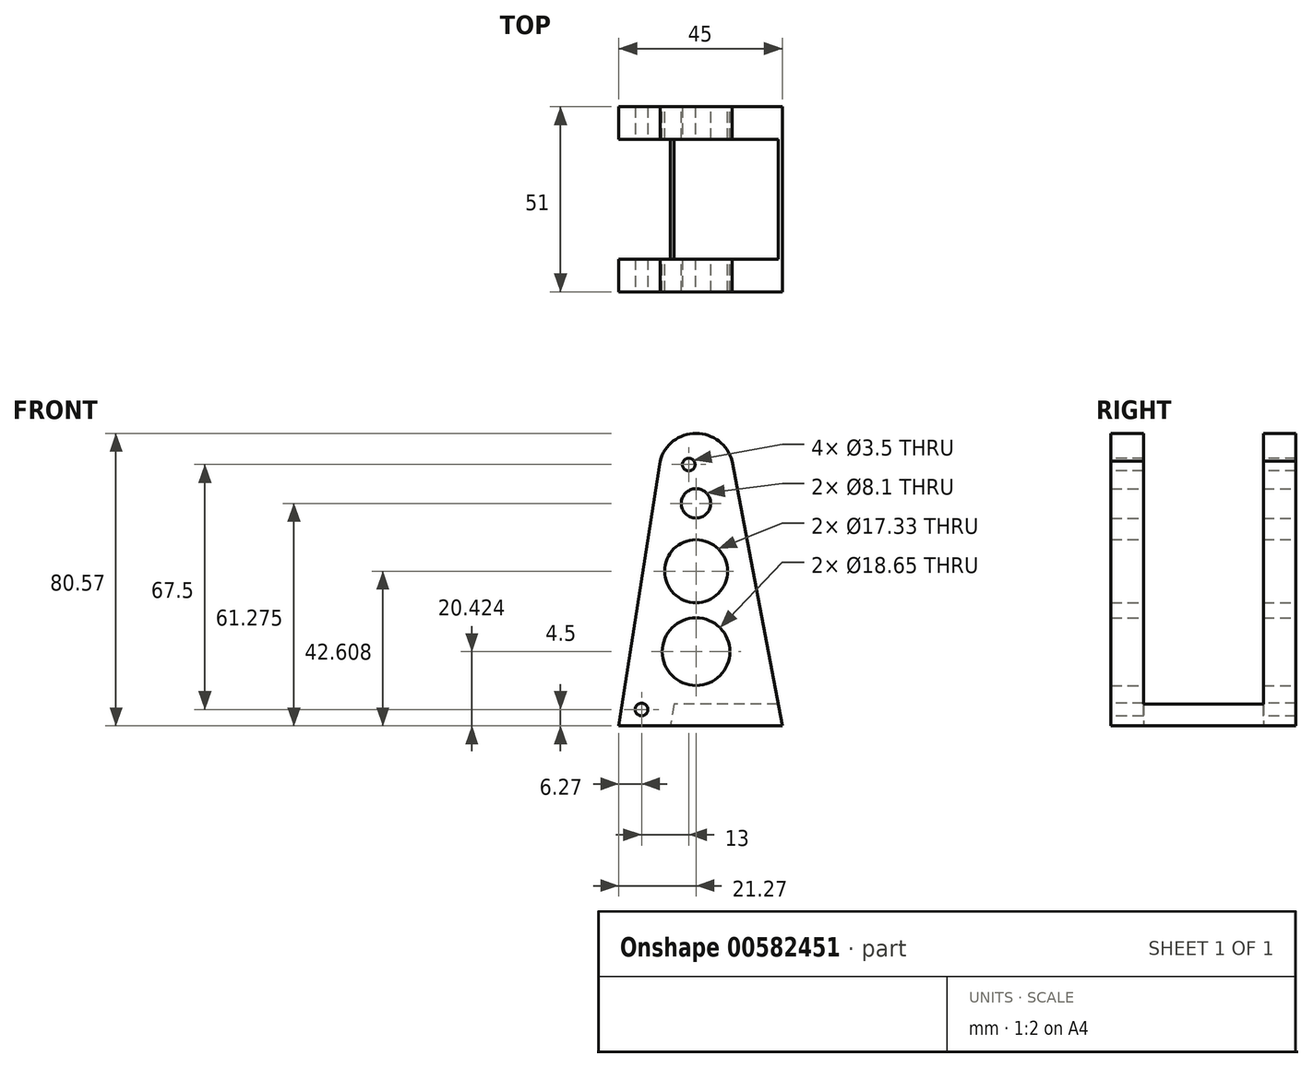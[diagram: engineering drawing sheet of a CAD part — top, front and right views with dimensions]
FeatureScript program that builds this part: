
annotation { "Feature Type Name" : "Feature", "Feature Type Description" : "" }
export const myFeature = defineFeature(function(context is Context, id is Id, definition is map)
    precondition{}
    {
        {
            var Q0;
            Q0=qCreatedBy(makeId("Front.planeOp"),FACE);
            var sketch = newSketch(context, id + "F0", { "sketchPlane" : qUnion([Q0])});
            skLineSegment(sketch, "E0", {"start": v(23.73, 0) * mm, "end": v(9.93, 72.97) * mm});
            skLineSegment(sketch, "E1", {"start": v(23.73, 0) * mm, "end": v(-21.27, 0) * mm});
            skLineSegment(sketch, "E2", {"start": v(-21.27, 0) * mm, "end": v(-9.93, 72.97) * mm});
            skArc(sketch, "E3", {"start": v(9.93, 72.97) * mm, "mid": v(0, 80.57) * mm, "end": v(-9.93, 72.97) * mm});
            skSolve(sketch);
        }
        {
            var Q0;
            Q0 = qSketchRegion(id + "F0", true);
            extrude(context, id + "F1", {"entities" : qUnion([Q0]), "endBound" : BoundingType.SYMMETRIC, "depth" : 51 * mm, "offsetDistance" : 25 * mm});
        }
        {
            var Q0;
            Q0=qCreatedBy(makeId("Front.planeOp"),FACE);
            var sketch = newSketch(context, id + "F2", { "sketchPlane" : qUnion([Q0])});
            skLineSegment(sketch, "E4", {"start": v(30, 6) * mm, "end": v(-6.1, 6) * mm});
            skLineSegment(sketch, "E5", {"start": v(-6.1, 6) * mm, "end": v(-7.03, 0) * mm});
            skLineSegment(sketch, "E6", {"start": v(-7.03, 0) * mm, "end": v(-30, 0) * mm});
            skLineSegment(sketch, "E7", {"start": v(-30, 0) * mm, "end": v(-30, 90) * mm});
            skLineSegment(sketch, "E8", {"start": v(-30, 90) * mm, "end": v(20, 90) * mm});
            skLineSegment(sketch, "E9", {"start": v(20, 90) * mm, "end": v(30, 6) * mm});
            skSolve(sketch);
        }
        {
            var Q0;
            Q0 = qSketchRegion(id + "F2", true);
            extrude(context, id + "F3", {"entities" : qUnion([Q0]), "endBound" : BoundingType.SYMMETRIC, "depth" : 33 * mm, "offsetDistance" : 25 * mm});
        }
        {
            var Q0;
            Q0=makeQuery(id+"F3.opExtrude","SWEPT_BODY",BODY,{"disambiguationData":[OSD([sQuery(id+"F2.wireOp",EDGE,"E4"),sQuery(id+"F2.wireOp",EDGE,"E5"),sQuery(id+"F2.wireOp",EDGE,"E6"),sQuery(id+"F2.wireOp",EDGE,"E7"),sQuery(id+"F2.wireOp",EDGE,"E8"),sQuery(id+"F2.wireOp",EDGE,"E9")])]});
            var Q1;
            Q1=makeQuery(id+"F1.opExtrude","SWEPT_BODY",BODY,{"disambiguationData":[OSD([sQuery(id+"F0.wireOp",EDGE,"E0"),sQuery(id+"F0.wireOp",EDGE,"E1"),sQuery(id+"F0.wireOp",EDGE,"E2"),sQuery(id+"F0.wireOp",EDGE,"E3")])]});
            booleanBodies(context, id + "F4", {"operationType" : BooleanOperationType.SUBTRACTION, "tools" : qUnion([Q0]), "targets" : qUnion([Q1])});
        }
        {
            var Q0;
            Q0=makeQuery(id+"F1.opExtrude","CAP_FACE",FACE,{"disambiguationData":[OSD([sQuery(id+"F0.wireOp",EDGE,"E0"),sQuery(id+"F0.wireOp",EDGE,"E1"),sQuery(id+"F0.wireOp",EDGE,"E2"),sQuery(id+"F0.wireOp",EDGE,"E3")])],"isStart":false});
            var sketch = newSketch(context, id + "F5", { "sketchPlane" : qUnion([Q0])});
            skLineSegment(sketch, "E10.bottom", {"start": v(-15, 4.5) * mm, "end": v(-2, 4.5) * mm});
            skLineSegment(sketch, "E10.top", {"start": v(-15, 72) * mm, "end": v(-2, 72) * mm});
            skLineSegment(sketch, "E10.left", {"start": v(-15, 4.5) * mm, "end": v(-15, 72) * mm});
            skLineSegment(sketch, "E10.right", {"start": v(-2, 4.5) * mm, "end": v(-2, 72) * mm});
            skSolve(sketch);
        }
        {
            var Q0;
            Q0=sQuery(id+"F5.wireOp",VERTEX,"E10.top.end");
            var Q1;
            Q1=sQuery(id+"F5.wireOp",VERTEX,"E10.left.start");
            var Q2;
            Q2=makeQuery(id+"F1.opExtrude","SWEPT_BODY",BODY,{"disambiguationData":[OSD([sQuery(id+"F0.wireOp",EDGE,"E0"),sQuery(id+"F0.wireOp",EDGE,"E1"),sQuery(id+"F0.wireOp",EDGE,"E2"),sQuery(id+"F0.wireOp",EDGE,"E3")])]});
            hole(context, id + "F6", {"style" : HoleStyle.SIMPLE, "endStyle" : HoleEndStyle.THROUGH, "holeDiameter" : 3.5 * mm, "majorDiameter" : 5 * mm, "tappedDepth" : 12 * mm, "tapClearance" : 3, "locations" : qUnion([Q0, Q1]), "scope" : qUnion([Q2])});
        }
        {
            var Q0;
            Q0=qCreatedBy(makeId("Front.planeOp"),FACE);
            var sketch = newSketch(context, id + "F7", { "sketchPlane" : qUnion([Q0])});
            skCircle(sketch, "E11", {"center": v(0, 42.6) * mm, "radius": 8.66 * mm});
            skCircle(sketch, "E12", {"center": v(0, 61.28) * mm, "radius": 4.05 * mm});
            skCircle(sketch, "E13", {"center": v(0, 20.42) * mm, "radius": 9.32 * mm});
            skSolve(sketch);
        }
        {
            var Q0;
            Q0 = qSketchRegion(id + "F7", true);
            extrude(context, id + "F8", {"entities" : qUnion([Q0]), "endBound" : BoundingType.SYMMETRIC, "depth" : 80 * mm, "offsetDistance" : 25 * mm});
        }
        {
            var Q0;
            Q0=makeQuery(id+"F8.opExtrude","SWEPT_BODY",BODY,{"disambiguationData":[OSD([sQuery(id+"F7.wireOp",EDGE,"E13")])]});
            var Q1;
            Q1=makeQuery(id+"F8.opExtrude","SWEPT_BODY",BODY,{"disambiguationData":[OSD([sQuery(id+"F7.wireOp",EDGE,"E11")])]});
            var Q2;
            Q2=makeQuery(id+"F8.opExtrude","SWEPT_BODY",BODY,{"disambiguationData":[OSD([sQuery(id+"F7.wireOp",EDGE,"E12")])]});
            var Q3;
            Q3=makeQuery(id+"F1.opExtrude","SWEPT_BODY",BODY,{"disambiguationData":[OSD([sQuery(id+"F0.wireOp",EDGE,"E0"),sQuery(id+"F0.wireOp",EDGE,"E1"),sQuery(id+"F0.wireOp",EDGE,"E2"),sQuery(id+"F0.wireOp",EDGE,"E3")])]});
            booleanBodies(context, id + "F9", {"operationType" : BooleanOperationType.SUBTRACTION, "tools" : qUnion([Q0, Q1, Q2]), "targets" : qUnion([Q3])});
        }
    });
